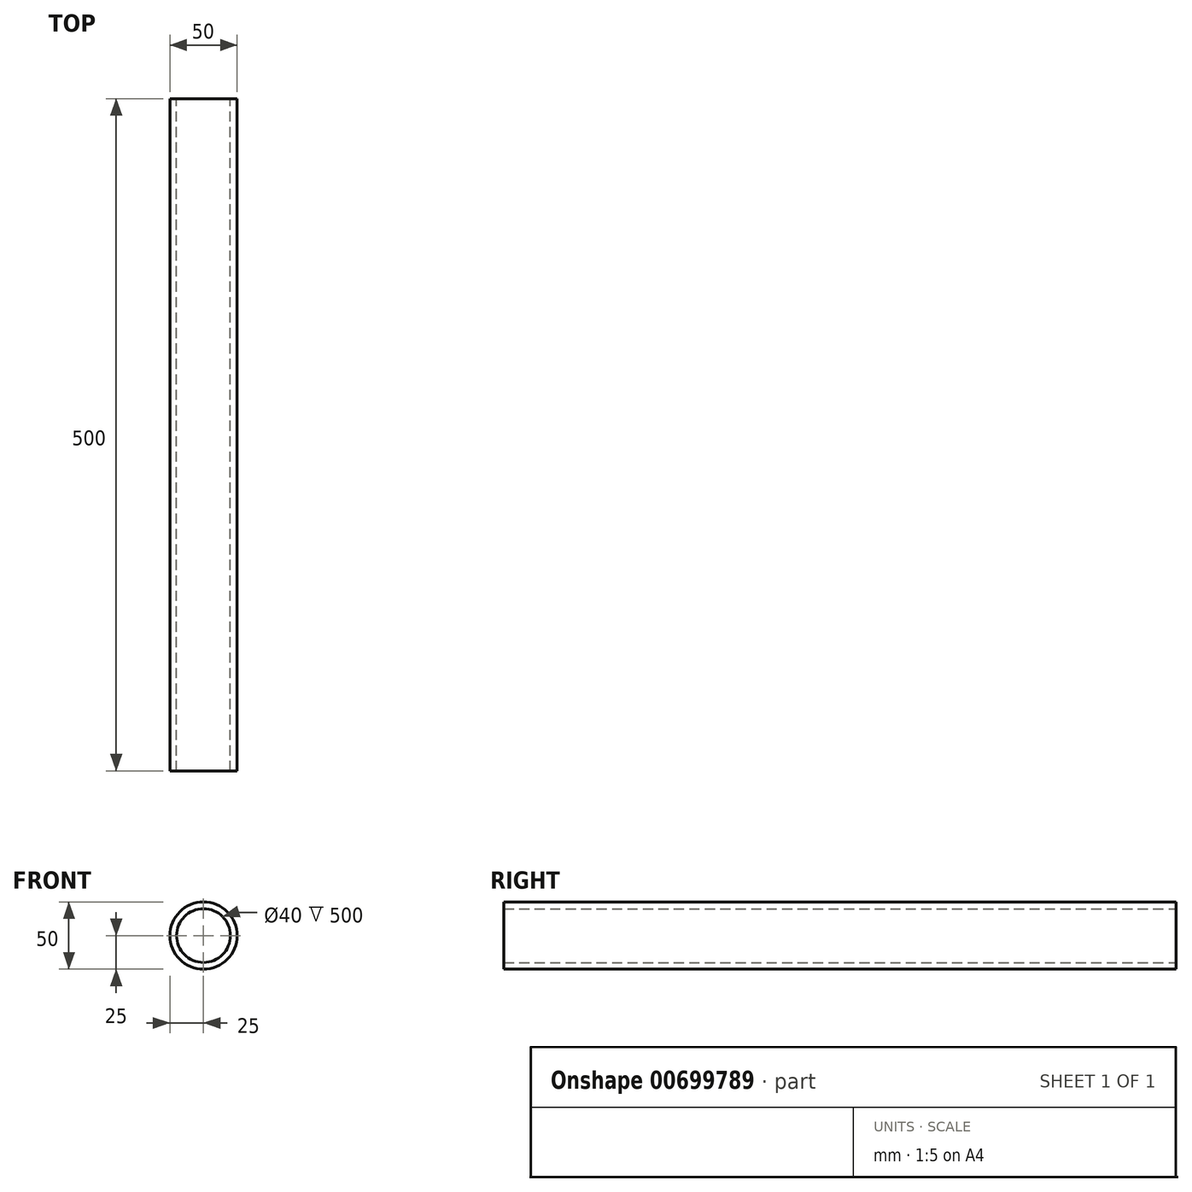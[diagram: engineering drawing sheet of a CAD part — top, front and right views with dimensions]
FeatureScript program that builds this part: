
annotation { "Feature Type Name" : "Feature", "Feature Type Description" : "" }
export const myFeature = defineFeature(function(context is Context, id is Id, definition is map)
    precondition{}
    {
        {
            var Q0;
            Q0=qCreatedBy(makeId("Front.planeOp"),FACE);
            var sketch = newSketch(context, id + "F0", { "sketchPlane" : qUnion([Q0])});
            skCircle(sketch, "E0", {"center": v(0, 0) * mm, "radius": 25 * mm});
            skSolve(sketch);
        }
        {
            var Q0;
            Q0 = qSketchRegion(id + "F0", true);
            extrude(context, id + "F1", {"entities" : qUnion([Q0]), "depth" : 500 * mm, "offsetDistance" : 25 * mm});
        }
        {
            var Q0;
            Q0=qCreatedBy(makeId("Front.planeOp"),FACE);
            var sketch = newSketch(context, id + "F2", { "sketchPlane" : qUnion([Q0])});
            skCircle(sketch, "E1", {"center": v(0, 0) * mm, "radius": 20 * mm});
            skSolve(sketch);
        }
        {
            var Q0;
            Q0=makeQuery(id+"F2.imprint","IMPRINT",FACE,{"disambiguationData":[TD([[makeQuery(id+"F2.imprint","IMPRINT",EDGE,{"derivedFrom":sQuery(id+"F2.wireOp",EDGE,"E1")}),1.0]])]});
            extrude(context, id + "F3", {"entities" : qUnion([Q0]), "operationType" : NewBodyOperationType.REMOVE, "depth" : 500 * mm, "offsetDistance" : 25 * mm});
        }
    });
